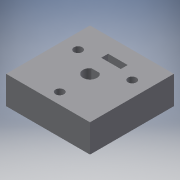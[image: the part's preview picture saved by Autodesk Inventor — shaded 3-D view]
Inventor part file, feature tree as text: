
AUTODESK INVENTOR PART (.ipt)
format: ipt  version: 2018.3 (Build 223284000, 284)  size: 112,640 bytes
history: native  units: mm
features: other x2, extrude x1, sketch x1
ambient origin geometry x8: Origin, YZ Plane, XZ Plane, XY Plane, X Axis, Y Axis, Z Axis, Center Point
bodies: Body1 (feature_tree)
feature tree (4):
  other  "Твердое тело1"
  other  "РабПлоскость2"
  extrude  "Выдавливание1"  Depth=15.0mm
  sketch  "Эскиз1"
